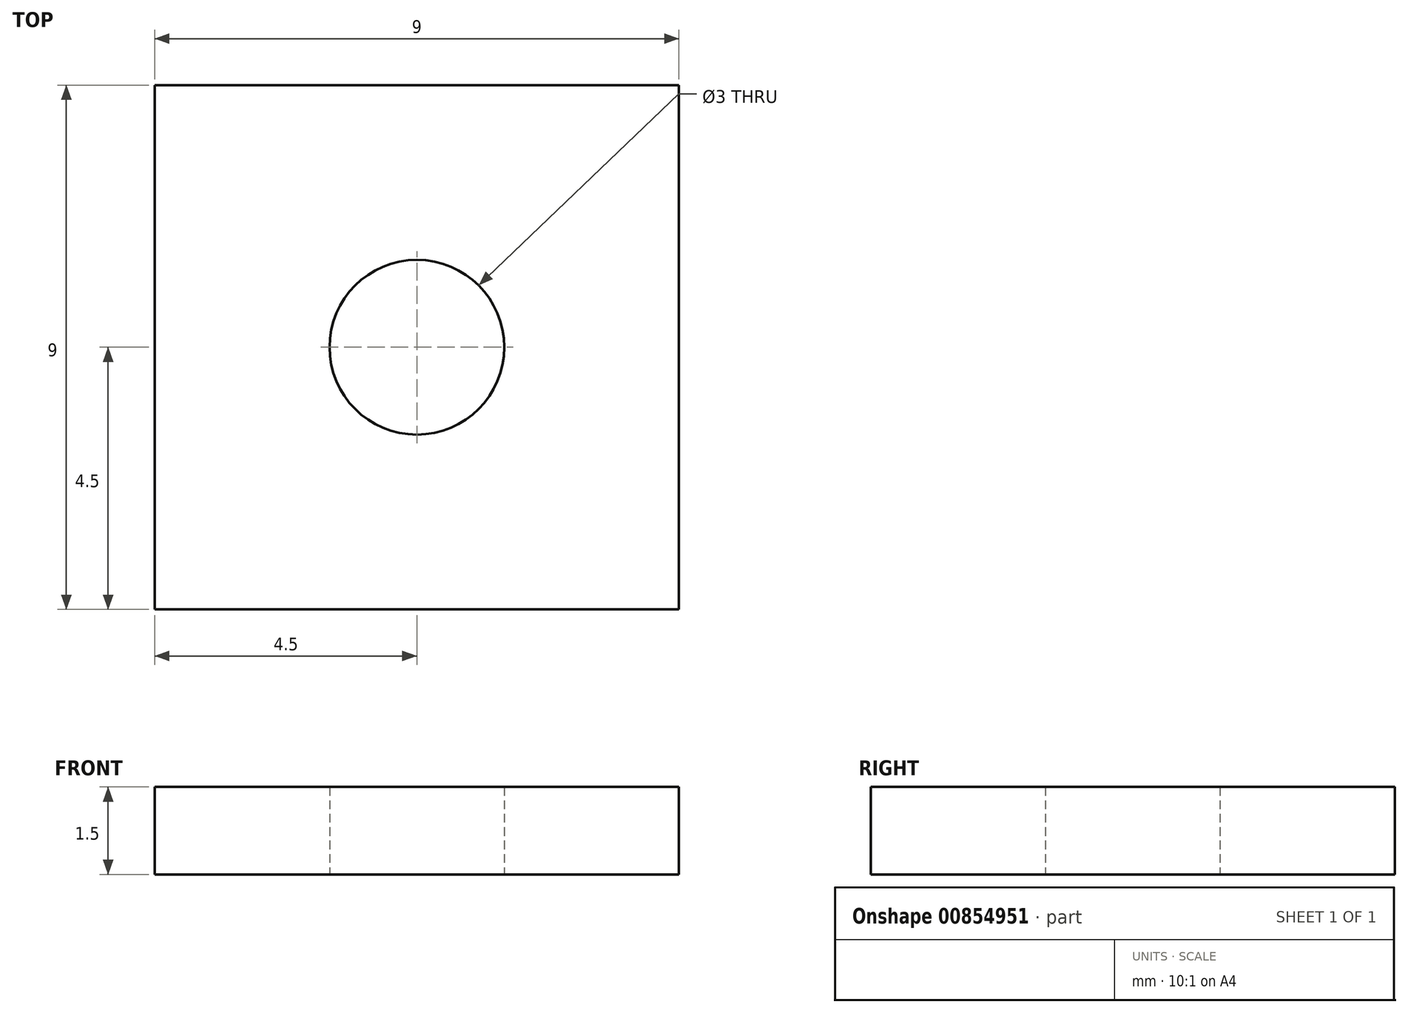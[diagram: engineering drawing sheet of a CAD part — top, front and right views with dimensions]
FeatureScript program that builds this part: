
annotation { "Feature Type Name" : "Feature", "Feature Type Description" : "" }
export const myFeature = defineFeature(function(context is Context, id is Id, definition is map)
    precondition{}
    {
        {
            var Q0;
            Q0=qCreatedBy(makeId("Top.planeOp"),FACE);
            var sketch = newSketch(context, id + "F0", { "sketchPlane" : qUnion([Q0])});
            skLineSegment(sketch, "E0.bottom", {"start": v(-4.5, 4.5) * mm, "end": v(4.5, 4.5) * mm});
            skLineSegment(sketch, "E0.top", {"start": v(-4.5, -4.5) * mm, "end": v(4.5, -4.5) * mm});
            skLineSegment(sketch, "E0.left", {"start": v(-4.5, 4.5) * mm, "end": v(-4.5, -4.5) * mm});
            skLineSegment(sketch, "E0.right", {"start": v(4.5, 4.5) * mm, "end": v(4.5, -4.5) * mm});
            skPoint(sketch, "E0.middle", {"position": v(0, 0) * mm});
            skCircle(sketch, "E1", {"center": v(0, 0) * mm, "radius": 1.5 * mm});
            skSolve(sketch);
        }
        {
            var Q0;
            Q0=makeQuery(id+"F0.imprint","IMPRINT",FACE,{"disambiguationData":[TD([[makeQuery(id+"F0.imprint","IMPRINT",EDGE,{"derivedFrom":sQuery(id+"F0.wireOp",EDGE,"E0.bottom")}),-1.0]])]});
            extrude(context, id + "F1", {"entities" : qUnion([Q0]), "depth" : 1.5 * mm, "offsetDistance" : 25 * mm});
        }
    });
